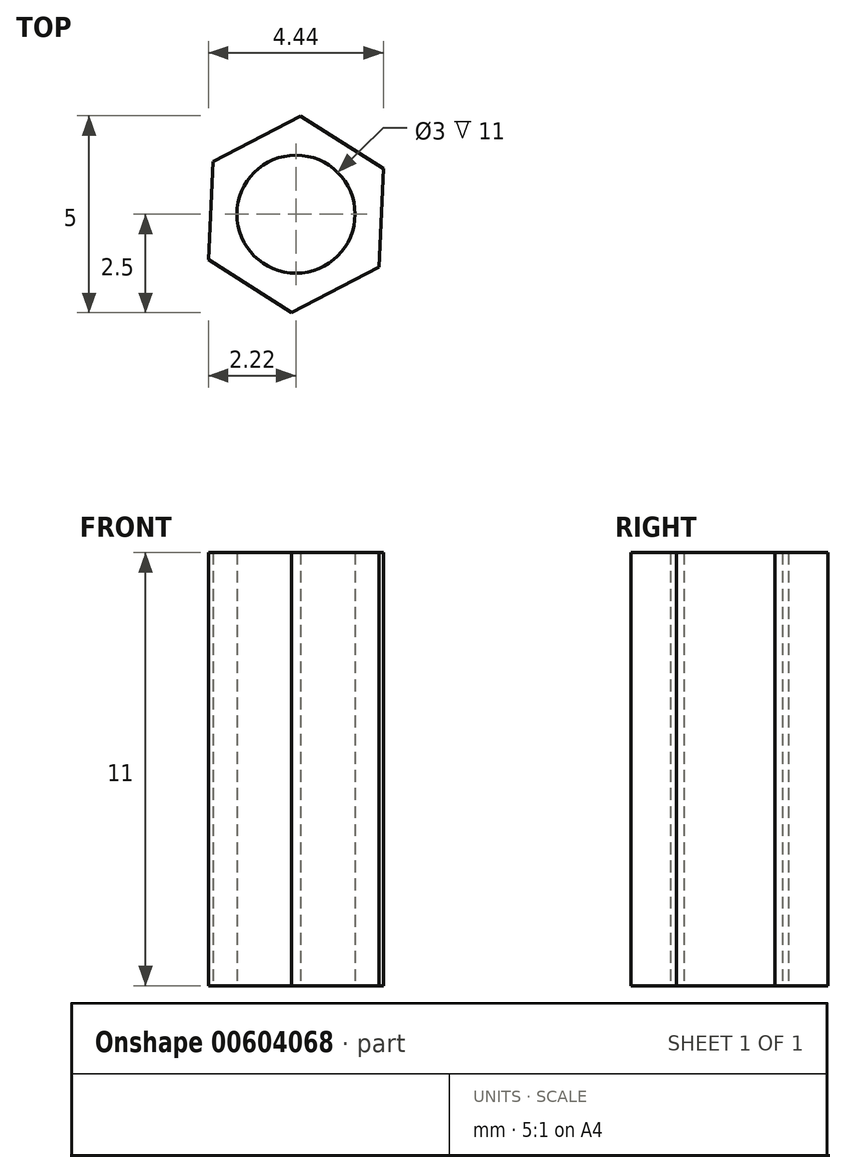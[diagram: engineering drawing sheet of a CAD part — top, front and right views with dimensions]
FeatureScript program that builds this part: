
annotation { "Feature Type Name" : "Feature", "Feature Type Description" : "" }
export const myFeature = defineFeature(function(context is Context, id is Id, definition is map)
    precondition{}
    {
        {
            var Q0;
            Q0=qCreatedBy(makeId("Top.planeOp"),FACE);
            var sketch = newSketch(context, id + "F0", { "sketchPlane" : qUnion([Q0])});
            skCircle(sketch, "E0.cCircle", {"center": v(0, 0) * mm, "radius": 2.5 * mm, "construction": true});
            skLineSegment(sketch, "E0.0", {"start": v(2.1, -1.34) * mm, "end": v(-0.1, -2.5) * mm});
            skLineSegment(sketch, "E0.1", {"start": v(-0.1, -2.5) * mm, "end": v(-2.22, -1.15) * mm});
            skLineSegment(sketch, "E0.2", {"start": v(-2.22, -1.15) * mm, "end": v(-2.1, 1.34) * mm});
            skLineSegment(sketch, "E0.3", {"start": v(-2.1, 1.34) * mm, "end": v(0.1, 2.5) * mm});
            skLineSegment(sketch, "E0.4", {"start": v(0.1, 2.5) * mm, "end": v(2.22, 1.15) * mm});
            skLineSegment(sketch, "E0.5", {"start": v(2.22, 1.15) * mm, "end": v(2.1, -1.34) * mm});
            skCircle(sketch, "E1", {"center": v(0, 0) * mm, "radius": 1.5 * mm});
            skSolve(sketch);
        }
        {
            var Q0;
            Q0=makeQuery(id+"F0.imprint","IMPRINT",FACE,{"disambiguationData":[TD([[makeQuery(id+"F0.imprint","IMPRINT",EDGE,{"derivedFrom":sQuery(id+"F0.wireOp",EDGE,"E0.0")}),-1.0]])]});
            extrude(context, id + "F1", {"entities" : qUnion([Q0]), "depth" : 11 * mm, "offsetDistance" : 25 * mm});
        }
    });
